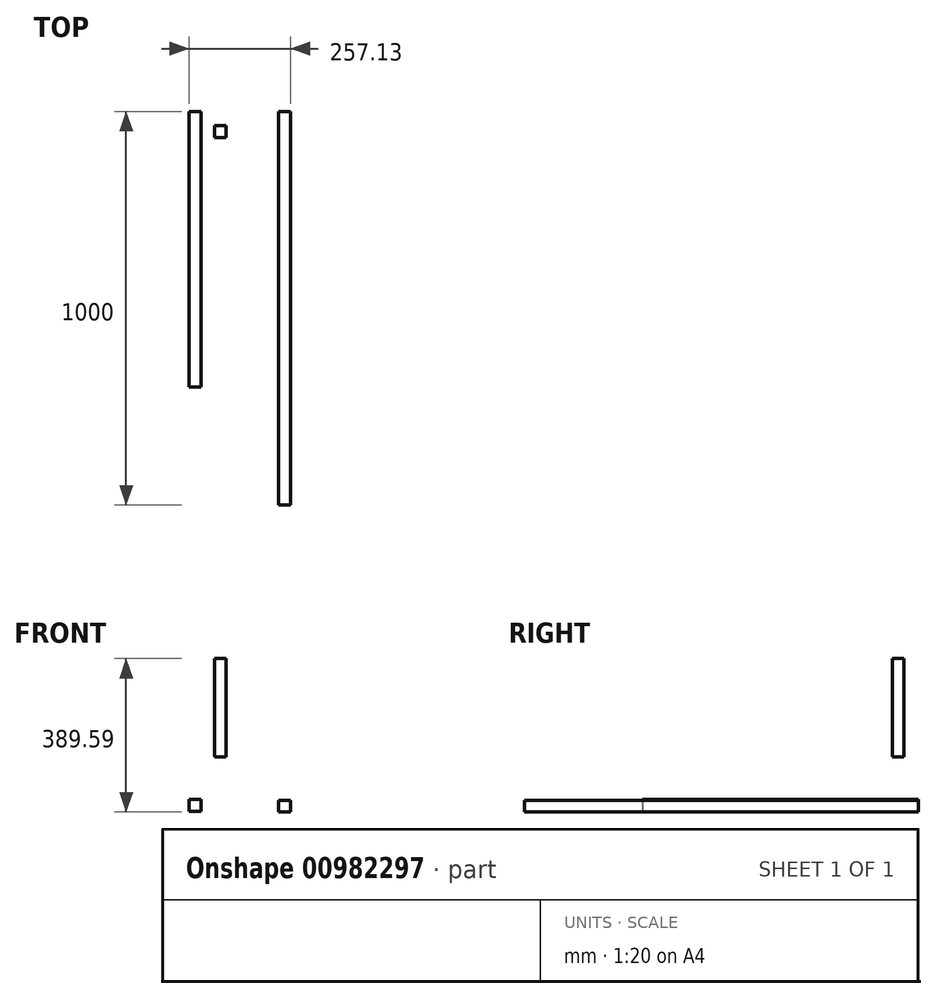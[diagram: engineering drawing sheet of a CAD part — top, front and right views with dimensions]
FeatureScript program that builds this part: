
annotation { "Feature Type Name" : "Feature", "Feature Type Description" : "" }
export const myFeature = defineFeature(function(context is Context, id is Id, definition is map)
    precondition{}
    {
        {
            var Q0;
            Q0=qCreatedBy(makeId("Top.planeOp"),FACE);
            var sketch = newSketch(context, id + "F0", { "sketchPlane" : qUnion([Q0])});
            skLineSegment(sketch, "E0.bottom", {"start": v(43.15, -65.93) * mm, "end": v(73.15, -65.93) * mm});
            skLineSegment(sketch, "E0.top", {"start": v(43.15, -35.93) * mm, "end": v(73.15, -35.93) * mm});
            skLineSegment(sketch, "E0.left", {"start": v(43.15, -65.93) * mm, "end": v(43.15, -35.93) * mm});
            skLineSegment(sketch, "E0.right", {"start": v(73.15, -65.93) * mm, "end": v(73.15, -35.93) * mm});
            skSolve(sketch);
        }
        {
            var Q0;
            Q0 = qSketchRegion(id + "F0", true);
            extrude(context, id + "F1", {"entities" : qUnion([Q0]), "depth" : 250 * mm, "offsetDistance" : 25 * mm});
        }
        {
            var Q0;
            Q0=qCreatedBy(makeId("Front.planeOp"),FACE);
            var sketch = newSketch(context, id + "F2", { "sketchPlane" : qUnion([Q0])});
            skLineSegment(sketch, "E1.bottom", {"start": v(206.42, -109.59) * mm, "end": v(236.42, -109.59) * mm});
            skLineSegment(sketch, "E1.top", {"start": v(206.42, -139.59) * mm, "end": v(236.42, -139.59) * mm});
            skLineSegment(sketch, "E1.left", {"start": v(206.42, -109.59) * mm, "end": v(206.42, -139.59) * mm});
            skLineSegment(sketch, "E1.right", {"start": v(236.42, -109.59) * mm, "end": v(236.42, -139.59) * mm});
            skLineSegment(sketch, "E2.bottom", {"start": v(-20.7, -107.6) * mm, "end": v(9.3, -107.6) * mm});
            skLineSegment(sketch, "E2.top", {"start": v(-20.7, -137.6) * mm, "end": v(9.3, -137.6) * mm});
            skLineSegment(sketch, "E2.left", {"start": v(-20.7, -107.6) * mm, "end": v(-20.7, -137.6) * mm});
            skLineSegment(sketch, "E2.right", {"start": v(9.3, -107.6) * mm, "end": v(9.3, -137.6) * mm});
            skSolve(sketch);
        }
        {
            var Q0;
            Q0=makeQuery(id+"F2.imprint","IMPRINT",FACE,{"disambiguationData":[TD([[makeQuery(id+"F2.imprint","IMPRINT",EDGE,{"derivedFrom":sQuery(id+"F2.wireOp",EDGE,"E1.bottom")}),-1.0]])]});
            extrude(context, id + "F3", {"entities" : qUnion([Q0]), "depth" : 1000 * mm, "offsetDistance" : 25 * mm});
        }
        {
            var Q0;
            Q0=makeQuery(id+"F2.imprint","IMPRINT",FACE,{"disambiguationData":[TD([[makeQuery(id+"F2.imprint","IMPRINT",EDGE,{"derivedFrom":sQuery(id+"F2.wireOp",EDGE,"E2.bottom")}),-1.0]])]});
            var Q1;
            Q1 = qConstructionFilter(qBodyType(qCreatedBy(id + "F2" ,EDGE), BodyType.WIRE), ConstructionObject.NO);
            extrude(context, id + "F4", {"entities" : qUnion([Q0]), "surfaceEntities" : qUnion([Q1]), "depth" : 700 * mm, "offsetDistance" : 25 * mm});
        }
    });
